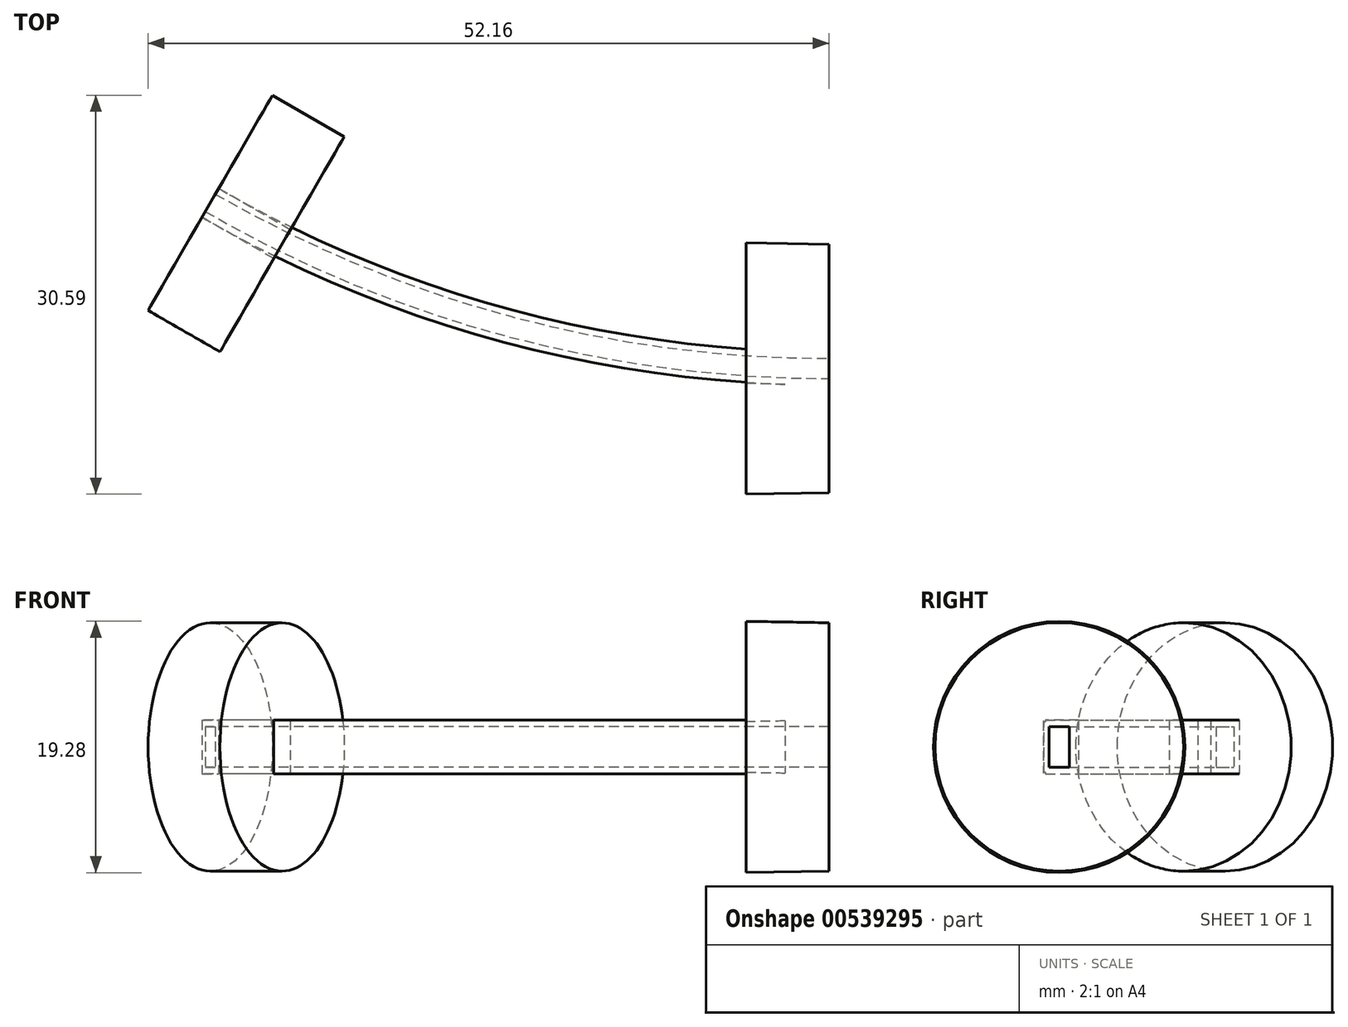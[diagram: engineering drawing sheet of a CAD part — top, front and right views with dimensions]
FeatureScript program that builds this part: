
annotation { "Feature Type Name" : "Feature", "Feature Type Description" : "" }
export const myFeature = defineFeature(function(context is Context, id is Id, definition is map)
    precondition{}
    {
        {
            var Q0;
            Q0=qCreatedBy(makeId("Top.planeOp"),FACE);
            var sketch = newSketch(context, id + "F0", { "sketchPlane" : qUnion([Q0])});
            skLineSegment(sketch, "E0", {"start": v(25.4, 0) * mm, "end": v(0, 0) * mm});
            skLineSegment(sketch, "E1", {"start": v(0, 0) * mm, "end": v(-22, 12.7) * mm});
            skArc(sketch, "E2", {"start": v(-22, 12.7) * mm, "mid": v(0.87, 3.23) * mm, "end": v(25.4, 0) * mm});
            skSolve(sketch);
        }
        {
            var Q0;
            Q0=sQuery(id+"F0.wireOp",EDGE,"E0");
            var Q1;
            Q1=sQuery(id+"F0.wireOp",VERTEX,"E0.start");
            cPlane(context, id + "F1", {"entities" : qUnion([Q0, Q1]), "cplaneType" : CPlaneType.LINE_POINT, "offset" : 25 * mm, "width" : 150 * mm, "height" : 150 * mm});
        }
        {
            var Q0;
            Q0=sQuery(id+"F0.wireOp",EDGE,"E1");
            var Q1;
            Q1=sQuery(id+"F0.wireOp",VERTEX,"E2.start");
            cPlane(context, id + "F2", {"entities" : qUnion([Q0, Q1]), "cplaneType" : CPlaneType.LINE_POINT, "offset" : 25 * mm, "width" : 150 * mm, "height" : 150 * mm});
        }
        {
            var Q0;
            Q0=qCreatedBy(id+"F2.planeOp",FACE);
            var sketch = newSketch(context, id + "F3", { "sketchPlane" : qUnion([Q0])});
            skLineSegment(sketch, "E3.bottom", {"start": v(-0.77, 1.55) * mm, "end": v(0.78, 1.55) * mm});
            skLineSegment(sketch, "E3.top", {"start": v(-0.78, -1.55) * mm, "end": v(0.77, -1.55) * mm});
            skLineSegment(sketch, "E3.left", {"start": v(-0.77, 1.55) * mm, "end": v(-0.78, -1.55) * mm});
            skLineSegment(sketch, "E3.right", {"start": v(0.78, 1.55) * mm, "end": v(0.77, -1.55) * mm});
            skPoint(sketch, "E3.middle", {"position": v(0, 0) * mm});
            skLineSegment(sketch, "E4.bottom", {"start": v(-1.27, 2.05) * mm, "end": v(1.28, 2.05) * mm});
            skLineSegment(sketch, "E4.top", {"start": v(-1.28, -2.05) * mm, "end": v(1.27, -2.05) * mm});
            skLineSegment(sketch, "E4.left", {"start": v(-1.27, 2.05) * mm, "end": v(-1.28, -2.05) * mm});
            skLineSegment(sketch, "E4.right", {"start": v(1.28, 2.05) * mm, "end": v(1.27, -2.05) * mm});
            skCircle(sketch, "E5", {"center": v(0, 0) * mm, "radius": 9.53 * mm});
            skSolve(sketch);
        }
        {
            var Q0;
            Q0=qCreatedBy(id+"F1.planeOp",FACE);
            var sketch = newSketch(context, id + "F4", { "sketchPlane" : qUnion([Q0])});
            skLineSegment(sketch, "E6.bottom", {"start": v(0.78, 1.55) * mm, "end": v(-0.77, 1.55) * mm});
            skLineSegment(sketch, "E6.top", {"start": v(0.78, -1.55) * mm, "end": v(-0.77, -1.55) * mm});
            skLineSegment(sketch, "E6.left", {"start": v(0.78, 1.55) * mm, "end": v(0.78, -1.55) * mm});
            skLineSegment(sketch, "E6.right", {"start": v(-0.77, 1.55) * mm, "end": v(-0.77, -1.55) * mm});
            skPoint(sketch, "E6.middle", {"position": v(0, 0) * mm});
            skLineSegment(sketch, "E7.bottom", {"start": v(1.28, 2.05) * mm, "end": v(-1.27, 2.05) * mm});
            skLineSegment(sketch, "E7.top", {"start": v(1.28, -2.05) * mm, "end": v(-1.27, -2.05) * mm});
            skLineSegment(sketch, "E7.left", {"start": v(1.28, 2.05) * mm, "end": v(1.28, -2.05) * mm});
            skLineSegment(sketch, "E7.right", {"start": v(-1.27, 2.05) * mm, "end": v(-1.27, -2.05) * mm});
            skCircle(sketch, "E8", {"center": v(0, 0) * mm, "radius": 9.53 * mm});
            skSolve(sketch);
        }
        {
            var Q0;
            Q0=makeQuery(id+"F4.imprint","IMPRINT",FACE,{"disambiguationData":[TD([[makeQuery(id+"F4.imprint","IMPRINT",EDGE,{"derivedFrom":sQuery(id+"F4.wireOp",EDGE,"E6.bottom")}),-1.0]])]});
            var Q1;
            Q1=makeQuery(id+"F3.imprint","IMPRINT",FACE,{"disambiguationData":[TD([[makeQuery(id+"F3.imprint","IMPRINT",EDGE,{"derivedFrom":sQuery(id+"F3.wireOp",EDGE,"E3.bottom")}),1.0]])]});
            var Q2;
            Q2=sQuery(id+"F0.wireOp",EDGE,"E2");
            sweep(context, id + "F5", {"profiles" : qUnion([Q0, Q1]), "path" : qUnion([Q2])});
        }
        {
            var Q0;
            Q0=makeQuery(id+"F5.opSweep","SWEPT_BODY",BODY,{"disambiguationData":[OSD([sQuery(id+"F0.wireOp",EDGE,"E2"),sQuery(id+"F3.wireOp",EDGE,"E3.bottom"),sQuery(id+"F3.wireOp",EDGE,"E3.top"),sQuery(id+"F3.wireOp",EDGE,"E3.left"),sQuery(id+"F3.wireOp",EDGE,"E3.right"),sQuery(id+"F3.wireOp",EDGE,"E4.bottom"),sQuery(id+"F3.wireOp",EDGE,"E4.top"),sQuery(id+"F3.wireOp",EDGE,"E4.left"),sQuery(id+"F3.wireOp",EDGE,"E4.right")])]});
            deleteBodies(context, id + "F6", {"entities" : qUnion([Q0])});
        }
        {
            var Q0;
            Q0=makeQuery(id+"F3.imprint","IMPRINT",FACE,{"disambiguationData":[TD([[makeQuery(id+"F3.imprint","IMPRINT",EDGE,{"derivedFrom":sQuery(id+"F3.wireOp",EDGE,"E4.bottom")}),1.0]])]});
            extrude(context, id + "F7", {"entities" : qUnion([Q0]), "oppositeDirection" : true, "depth" : 6.35 * mm, "offsetDistance" : 25 * mm});
        }
        {
            var Q0;
            Q0=makeQuery(id+"F4.imprint","IMPRINT",FACE,{"disambiguationData":[TD([[makeQuery(id+"F4.imprint","IMPRINT",EDGE,{"derivedFrom":sQuery(id+"F4.wireOp",EDGE,"E7.bottom")}),-1.0]])]});
            extrude(context, id + "F8", {"entities" : qUnion([Q0]), "operationType" : NewBodyOperationType.ADD, "depth" : 6.35 * mm, "offsetDistance" : 25 * mm, "hasDraft" : true, "draftAngle" : 1 * degree});
        }
    });
